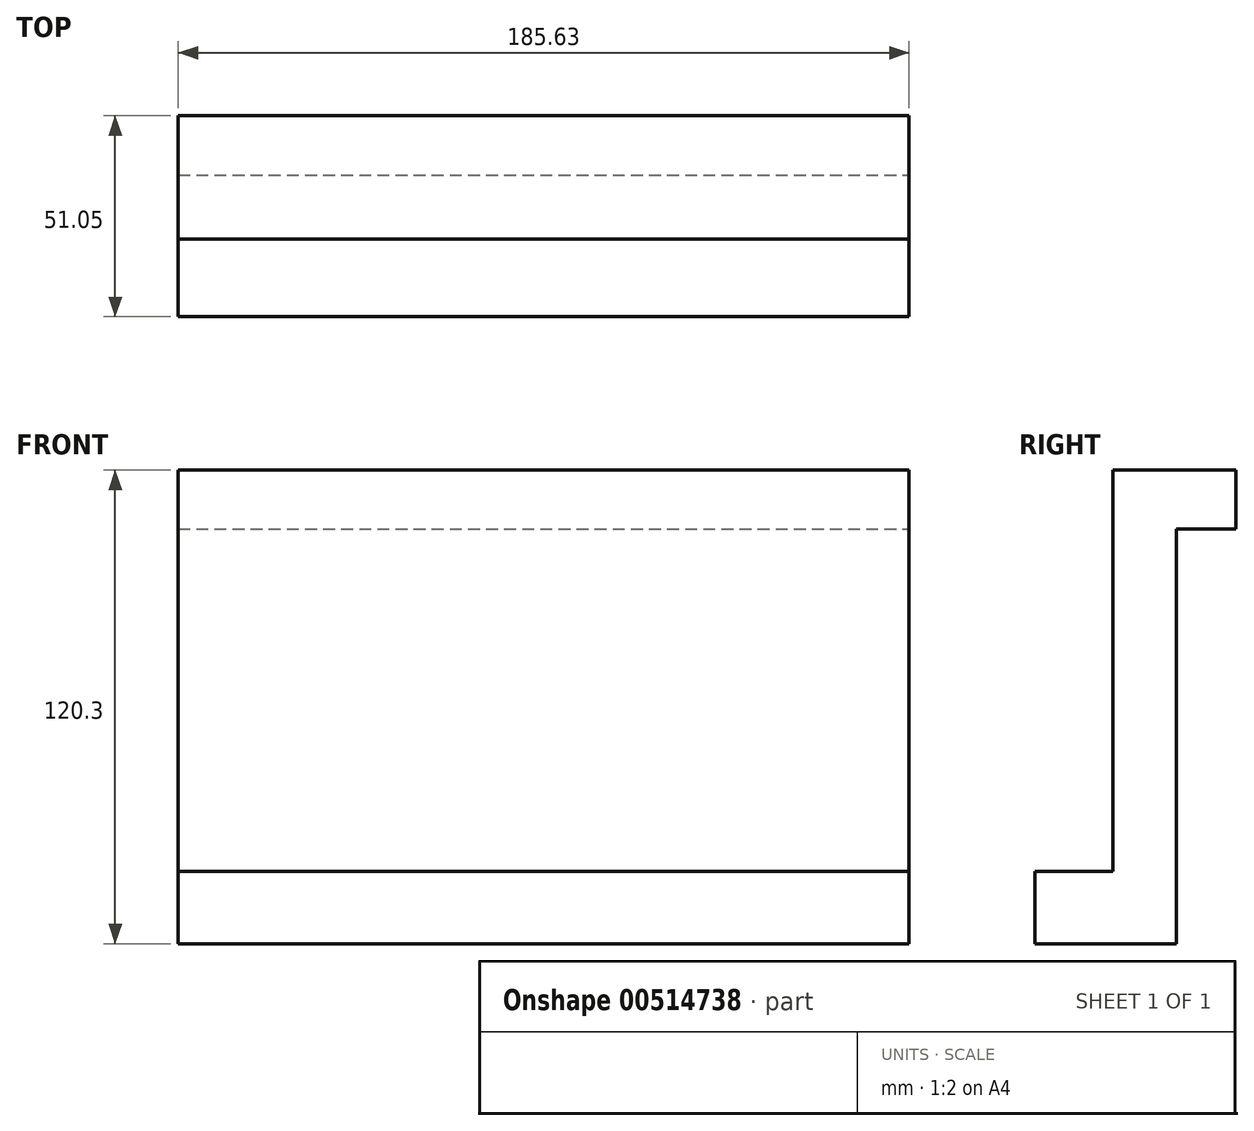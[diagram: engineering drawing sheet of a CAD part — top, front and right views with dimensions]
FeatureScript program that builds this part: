
annotation { "Feature Type Name" : "Feature", "Feature Type Description" : "" }
export const myFeature = defineFeature(function(context is Context, id is Id, definition is map)
    precondition{}
    {
        {
            var Q0;
            Q0=qCreatedBy(makeId("Front.planeOp"),FACE);
            var sketch = newSketch(context, id + "F0", { "sketchPlane" : qUnion([Q0])});
            skLineSegment(sketch, "E0.bottom", {"start": v(-72.7, 37.09) * mm, "end": v(112.93, 37.09) * mm});
            skLineSegment(sketch, "E0.top", {"start": v(-72.7, -83.2) * mm, "end": v(112.93, -83.2) * mm});
            skLineSegment(sketch, "E0.left", {"start": v(-72.7, 37.09) * mm, "end": v(-72.7, -83.2) * mm});
            skLineSegment(sketch, "E0.right", {"start": v(112.93, 37.09) * mm, "end": v(112.93, -83.2) * mm});
            skSolve(sketch);
        }
        {
            var Q0;
            Q0 = qSketchRegion(id + "F0", true);
            extrude(context, id + "F1", {"entities" : qUnion([Q0]), "depth" : 51.05 * mm, "offsetDistance" : 25.4 * mm});
        }
        {
            var Q0;
            Q0=makeQuery(id+"F1.opExtrude","SWEPT_FACE",FACE,{"disambiguationData":[OSD([sQuery(id+"F0.wireOp",EDGE,"E0.right")])]});
            var sketch = newSketch(context, id + "F2", { "sketchPlane" : qUnion([Q0])});
            skLineSegment(sketch, "E1.bottom", {"start": v(-51.05, 37.09) * mm, "end": v(-31.29, 37.09) * mm});
            skLineSegment(sketch, "E1.top", {"start": v(-51.05, -64.84) * mm, "end": v(-31.29, -64.84) * mm});
            skLineSegment(sketch, "E1.left", {"start": v(-51.05, 37.09) * mm, "end": v(-51.05, -64.84) * mm});
            skLineSegment(sketch, "E1.right", {"start": v(-31.29, 37.09) * mm, "end": v(-31.29, -64.84) * mm});
            skSolve(sketch);
        }
        {
            var Q0;
            Q0 = qSketchRegion(id + "F2", true);
            extrude(context, id + "F3", {"entities" : qUnion([Q0]), "operationType" : NewBodyOperationType.REMOVE, "oppositeDirection" : true, "depth" : 220.22 * mm, "offsetDistance" : 25.4 * mm});
        }
        {
            var Q0;
            Q0=makeQuery(id+"F1.opExtrude","SWEPT_FACE",FACE,{"disambiguationData":[OSD([sQuery(id+"F0.wireOp",EDGE,"E0.right")])]});
            var sketch = newSketch(context, id + "F4", { "sketchPlane" : qUnion([Q0])});
            skLineSegment(sketch, "E2.bottom", {"start": v(0, -83.2) * mm, "end": v(-15.06, -83.2) * mm});
            skLineSegment(sketch, "E2.top", {"start": v(0, 22.22) * mm, "end": v(-15.06, 22.22) * mm});
            skLineSegment(sketch, "E2.left", {"start": v(0, -83.2) * mm, "end": v(0, 22.22) * mm});
            skLineSegment(sketch, "E2.right", {"start": v(-15.06, -83.2) * mm, "end": v(-15.06, 22.22) * mm});
            skSolve(sketch);
        }
        {
            var Q0;
            Q0 = qSketchRegion(id + "F4", true);
            extrude(context, id + "F5", {"entities" : qUnion([Q0]), "operationType" : NewBodyOperationType.REMOVE, "oppositeDirection" : true, "depth" : 191.26 * mm, "offsetDistance" : 25.4 * mm});
        }
    });
